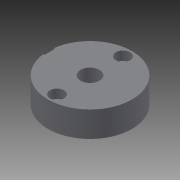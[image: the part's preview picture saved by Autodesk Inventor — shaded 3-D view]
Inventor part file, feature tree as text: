
AUTODESK INVENTOR PART (.ipt)
format: ipt  version: 2014 (Build 180170000, 170)  size: 226,304 bytes
history: native  units: in
note: dims shown in document units (in); Inventor stores cm internally (conversion verified against a paired STEP export)
features: other x189, sketch x10, hole x7, revolve x3, thread x1
ambient origin geometry x8: Origin, YZ Plane, XZ Plane, XY Plane, X Axis, Y Axis, Z Axis, Center Point
bodies: Solid1 (feature_tree)
feature tree (210):
  revolve  "Revolution1"  Angle=360.0deg
  revolve  "Revolution2"  Angle=360.0deg
  thread  "Thread1"  [1 undecoded]
  hole  "Hole1"  [1 undecoded]
  revolve  "Revolution3"  [1 undecoded]
  hole  "Hole2"  [1 undecoded]
  hole  "Hole3"  [1 undecoded]
  hole  "Hole4"  [1 undecoded]
  hole  "Hole5"  [1 undecoded]
  hole  "Hole6"  [1 undecoded]
  hole  "Hole7"  [1 undecoded]
  other  "a1_XY"
  other  "a1_YZ"
  other  "a1_ZX"
  other  "a1_X"
  other  "a1_Y"
  other  "a1_Z"
  other  "a1_Center"
  other  "a2_XY"
  other  "a2_YZ"
  other  "a2_ZX"
  other  "a2_X"
  other  "a2_Y"
  other  "a2_Z"
  other  "a2_Center"
  other  "ar3_XY"
  other  "ar3_YZ"
  other  "ar3_ZX"
  other  "ar3_X"
  other  "ar3_Y"
  other  "ar3_Z"
  other  "ar3_Center"
  other  "ar4_XY"
  other  "ar4_YZ"
  other  "ar4_ZX"
  other  "ar4_X"
  other  "ar4_Y"
  other  "ar4_Z"
  other  "ar4_Center"
  other  "ar5_XY"
  other  "ar5_YZ"
  other  "ar5_ZX"
  other  "ar5_X"
  other  "ar5_Y"
  other  "ar5_Z"
  other  "ar5_Center"
  other  "ar6_XY"
  other  "ar6_YZ"
  other  "ar6_ZX"
  other  "ar6_X"
  other  "ar6_Y"
  other  "ar6_Z"
  other  "ar6_Center"
  other  "b1_XY"
  other  "b1_YZ"
  other  "b1_ZX"
  other  "b1_X"
  other  "b1_Y"
  other  "b1_Z"
  other  "b1_Center"
  other  "c1_XY"
  other  "c1_YZ"
  other  "c1_ZX"
  other  "c1_X"
  other  "c1_Y"
  other  "c1_Z"
  other  "c1_Center"
  other  "c2_XY"
  other  "c2_YZ"
  other  "c2_ZX"
  other  "c2_X"
  other  "c2_Y"
  other  "c2_Z"
  other  "c2_Center"
  other  "d1_XY"
  other  "d1_YZ"
  other  "d1_ZX"
  other  "d1_X"
  other  "d1_Y"
  other  "d1_Z"
  other  "d1_Center"
  other  "d2_XY"
  other  "d2_YZ"
  other  "d2_ZX"
  other  "d2_X"
  other  "d2_Y"
  other  "d2_Z"
  other  "d2_Center"
  other  "j_XY"
  other  "j_YZ"
  other  "j_ZX"
  other  "j_X"
  other  "j_Y"
  other  "j_Z"
  other  "j_Center"
  other  "k1_XY"
  other  "k1_YZ"
  other  "k1_ZX"
  other  "k1_X"
  other  "k1_Y"
  other  "k1_Z"
  other  "k1_Center"
  other  "k2_XY"
  other  "k2_YZ"
  other  "k2_ZX"
  other  "k2_X"
  other  "k2_Y"
  other  "k2_Z"
  other  "k2_Center"
  other  "l1_XY"
  other  "l1_YZ"
  other  "l1_ZX"
  other  "l1_X"
  other  "l1_Y"
  other  "l1_Z"
  other  "l1_Center"
  other  "l2_XY"
  other  "l2_YZ"
  other  "l2_ZX"
  other  "l2_X"
  other  "l2_Y"
  other  "l2_Z"
  other  "l2_Center"
  other  "rg_XY"
  other  "rg_YZ"
  other  "rg_ZX"
  other  "rg_X"
  other  "rg_Y"
  other  "rg_Z"
  other  "rg_Center"
  other  "rh_XY"
  other  "rh_YZ"
  other  "rh_ZX"
  other  "rh_X"
  other  "rh_Y"
  other  "rh_Z"
  other  "rh_Center"
  other  "to_dummy_XY"
  other  "to_dummy_YZ"
  other  "to_dummy_ZX"
  other  "to_dummy_X"
  other  "to_dummy_Y"
  other  "to_dummy_Z"
  other  "to_dummy_Center"
  other  "to_nut_XY"
  other  "to_nut_YZ"
  other  "to_nut_ZX"
  other  "to_nut_X"
  other  "to_nut_Y"
  other  "to_nut_Z"
  other  "to_nut_Center"
  other  "to_rod_XY"
  other  "to_rod_YZ"
  other  "to_rod_ZX"
  other  "to_rod_X"
  other  "to_rod_Y"
  other  "to_rod_Z"
  other  "to_rod_Center"
  other  "to_tube_XY"
  other  "to_tube_YZ"
  other  "to_tube_ZX"
  other  "to_tube_X"
  other  "to_tube_Y"
  other  "to_tube_Z"
  other  "to_tube_Center"
  other  "to_wiper_XY"
  other  "to_wiper_YZ"
  other  "to_wiper_ZX"
  other  "to_wiper_X"
  other  "to_wiper_Y"
  other  "to_wiper_Z"
  other  "to_wiper_Center"
  other  "track1_XY"
  other  "track1_YZ"
  other  "track1_ZX"
  other  "track1_X"
  other  "track1_Y"
  other  "track1_Z"
  other  "track1_Center"
  other  "track2_XY"
  other  "track2_YZ"
  other  "track2_ZX"
  other  "track2_X"
  other  "track2_Y"
  other  "track2_Z"
  other  "track2_Center"
  other  "track3_XY"
  other  "track3_YZ"
  other  "track3_ZX"
  other  "track3_X"
  other  "track3_Y"
  other  "track3_Z"
  other  "track3_Center"
  other  "track4_XY"
  other  "track4_YZ"
  other  "track4_ZX"
  other  "track4_X"
  other  "track4_Y"
  other  "track4_Z"
  other  "track4_Center"
  sketch  "Sketch_1"  dims[d0=360.0deg d1=360.0deg]
  sketch  "Sketch_37"
  sketch  "Sketch3"  dims[d2=0.2in d3=0.06in]
  sketch  "Sketch_9"  dims[d33=0.12in d34=0.75in d35=0.375in d36=0.25in d37=0.5635in d38=0.1in d39=0.0in]
  sketch  "Sketch5"  dims[d4=0.252in d5=0.75in d6=0.375in d7=0.25in d8=0.5635in d9=0.34in d10=0.0in d11=360.0deg]
  sketch  "Sketch6"  dims[d12=0.12in d13=0.75in d14=0.188in d15=0.12in d16=0.5635in d17=0.34in d18=0.0in]
  sketch  "Sketch7"  dims[d19=0.12in d20=0.75in d21=0.188in d22=0.12in d23=0.5635in d24=0.34in d25=0.0in]
  sketch  "Sketch8"  dims[d26=0.12in d27=0.75in d28=0.375in d29=0.25in d30=0.5635in d31=0.1in d32=0.0in]
  sketch  "Sketch9"  dims[d40=0.12in d41=0.75in d42=0.375in d43=0.25in d44=0.5635in d45=0.1in d46=0.0in]
  sketch  "Sketch10"  dims[d47=0.12in d48=0.75in d49=0.375in d50=0.25in d51=0.5635in d52=0.1in d53=0.0in]
note: 9 required parameter values undecoded (feature->parameter linkage not recoverable at this tier; creation-order binding heuristic only, values carry confidence <= 0.55)
